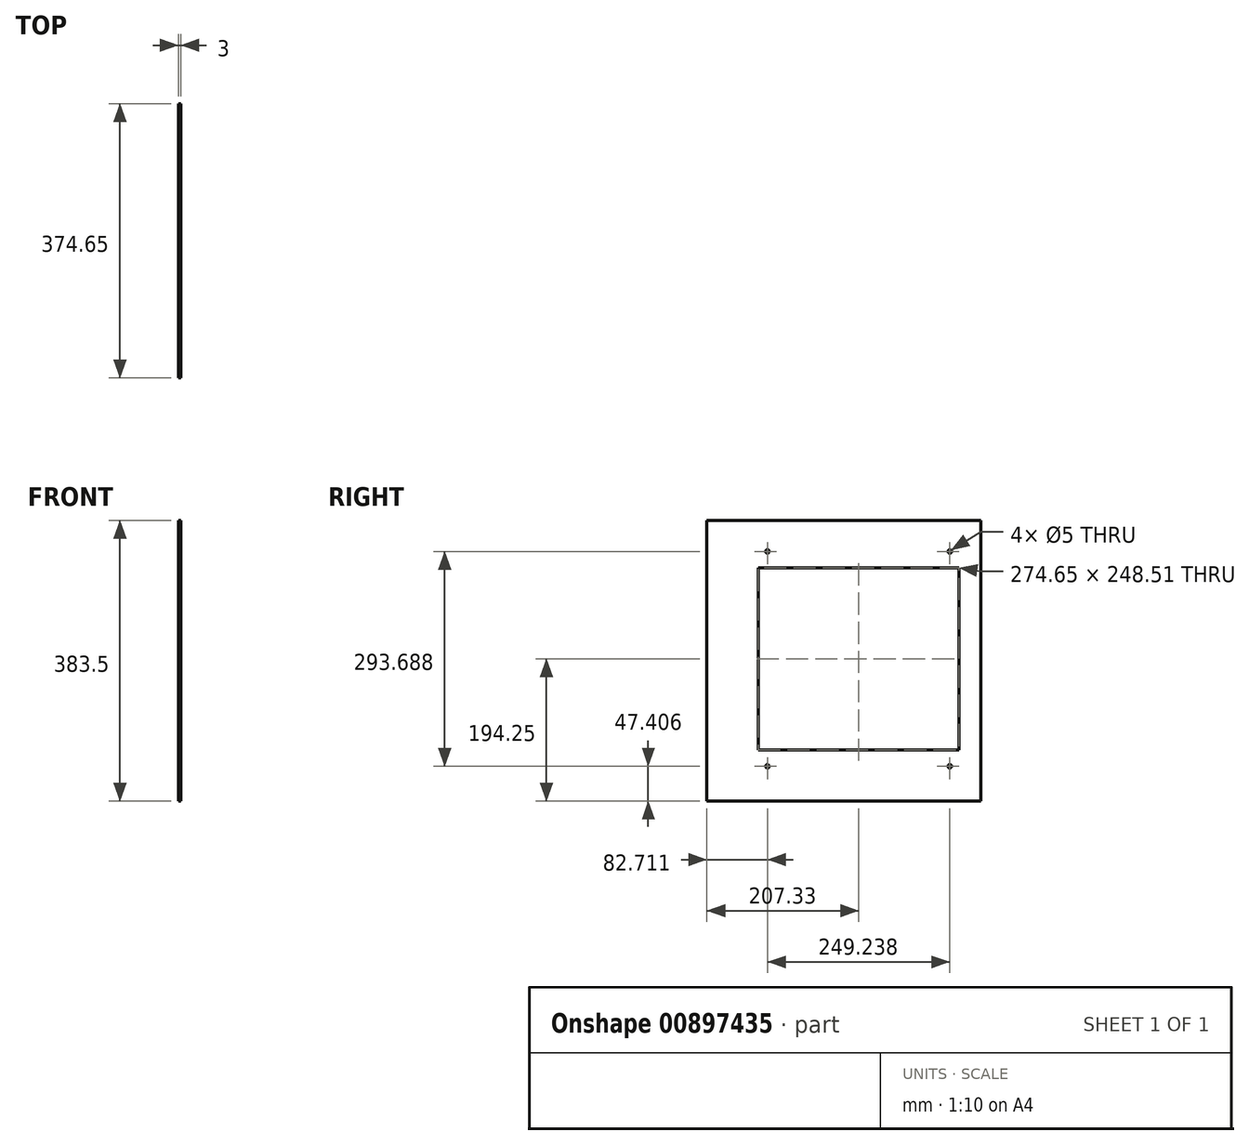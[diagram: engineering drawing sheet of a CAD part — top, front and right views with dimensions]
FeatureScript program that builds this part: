
annotation { "Feature Type Name" : "Feature", "Feature Type Description" : "" }
export const myFeature = defineFeature(function(context is Context, id is Id, definition is map)
    precondition{}
    {
        {
            var Q0;
            Q0=qCreatedBy(makeId("Right.planeOp"),FACE);
            var sketch = newSketch(context, id + "F0", { "sketchPlane" : qUnion([Q0])});
            skLineSegment(sketch, "E0.bottom", {"start": v(-140.5, 179.39) * mm, "end": v(140.5, 179.39) * mm, "construction": true});
            skLineSegment(sketch, "E0.top", {"start": v(-140.5, -179.39) * mm, "end": v(140.5, -179.39) * mm, "construction": true});
            skLineSegment(sketch, "E0.left", {"start": v(-140.5, 179.39) * mm, "end": v(-140.5, -179.39) * mm, "construction": true});
            skLineSegment(sketch, "E0.right", {"start": v(140.5, 179.39) * mm, "end": v(140.5, -179.39) * mm, "construction": true});
            skPoint(sketch, "E0.middle", {"position": v(0, 0) * mm});
            skLineSegment(sketch, "E1.bottom", {"start": v(-124.62, 146.84) * mm, "end": v(124.62, 146.84) * mm, "construction": true});
            skLineSegment(sketch, "E1.top", {"start": v(-124.62, -146.84) * mm, "end": v(124.62, -146.84) * mm, "construction": true});
            skLineSegment(sketch, "E1.left", {"start": v(-124.62, 146.84) * mm, "end": v(-124.62, -146.84) * mm, "construction": true});
            skLineSegment(sketch, "E1.right", {"start": v(124.62, 146.84) * mm, "end": v(124.62, -146.84) * mm, "construction": true});
            skCircle(sketch, "E2", {"center": v(-124.62, 146.84) * mm, "radius": 2.5 * mm});
            skCircle(sketch, "E3", {"center": v(124.62, 146.84) * mm, "radius": 2.5 * mm});
            skCircle(sketch, "E4", {"center": v(-124.62, -146.84) * mm, "radius": 2.5 * mm});
            skCircle(sketch, "E5", {"center": v(124.62, -146.84) * mm, "radius": 2.5 * mm});
            skLineSegment(sketch, "E6.bottom", {"start": v(-207.32, 189.25) * mm, "end": v(167.33, 189.25) * mm});
            skLineSegment(sketch, "E6.top", {"start": v(-207.33, -194.25) * mm, "end": v(167.32, -194.25) * mm});
            skLineSegment(sketch, "E6.left", {"start": v(-207.32, 189.25) * mm, "end": v(-207.33, -194.25) * mm});
            skLineSegment(sketch, "E6.right", {"start": v(167.33, 189.25) * mm, "end": v(167.32, -194.25) * mm});
            skPoint(sketch, "E6.middle", {"position": v(-20, -2.5) * mm});
            skLineSegment(sketch, "E7.bottom", {"start": v(-137.32, 124.25) * mm, "end": v(137.33, 124.25) * mm});
            skLineSegment(sketch, "E7.top", {"start": v(-137.33, -124.25) * mm, "end": v(137.32, -124.25) * mm});
            skLineSegment(sketch, "E7.left", {"start": v(-137.32, 124.25) * mm, "end": v(-137.33, -124.25) * mm});
            skLineSegment(sketch, "E7.right", {"start": v(137.33, 124.25) * mm, "end": v(137.32, -124.25) * mm});
            skSolve(sketch);
        }
        {
            var Q0;
            Q0 = qSketchRegion(id + "F0", true);
            extrude(context, id + "F1", {"entities" : qUnion([Q0]), "depth" : 3 * mm, "offsetDistance" : 25 * mm});
        }
    });
